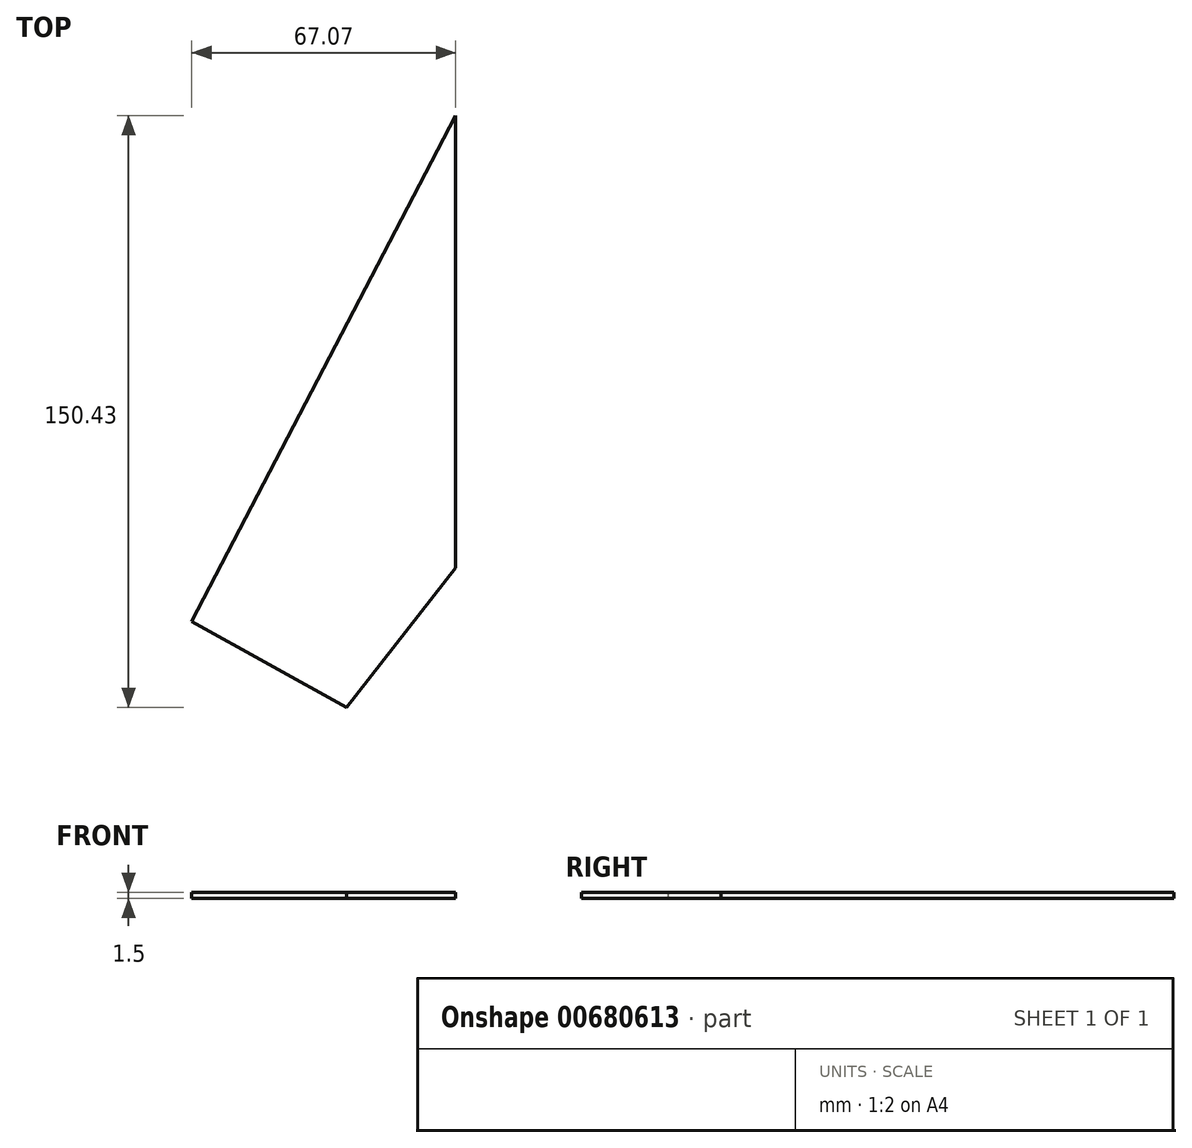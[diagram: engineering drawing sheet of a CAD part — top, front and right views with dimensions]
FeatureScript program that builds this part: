
annotation { "Feature Type Name" : "Feature", "Feature Type Description" : "" }
export const myFeature = defineFeature(function(context is Context, id is Id, definition is map)
    precondition{}
    {
        {
            var Q0;
            Q0=qCreatedBy(makeId("Top.planeOp"),FACE);
            var sketch = newSketch(context, id + "F0", { "sketchPlane" : qUnion([Q0])});
            skLineSegment(sketch, "E0", {"start": v(0, 0) * mm, "end": v(0, 115) * mm});
            skLineSegment(sketch, "E1", {"start": v(0, 115) * mm, "end": v(-67.07, -13.55) * mm});
            skLineSegment(sketch, "E2", {"start": v(-67.07, -13.55) * mm, "end": v(-27.75, -35.43) * mm});
            skLineSegment(sketch, "E3", {"start": v(-27.75, -35.43) * mm, "end": v(0, 0) * mm});
            skPoint(sketch, "E4", {"position": v(-60, 0) * mm});
            skSolve(sketch);
        }
        {
            var Q0;
            Q0 = qSketchRegion(id + "F0", true);
            extrude(context, id + "F1", {"entities" : qUnion([Q0]), "depth" : 1.5 * mm, "offsetDistance" : 25 * mm});
        }
    });
